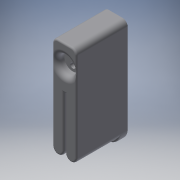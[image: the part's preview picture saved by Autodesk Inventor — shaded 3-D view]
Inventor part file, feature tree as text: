
AUTODESK INVENTOR PART (.ipt)
format: ipt  version: 2019 (Build 230136000, 136)  size: 194,560 bytes
history: native  units: mm
features: fillet x4, extrude x3, sketch x3
ambient origin geometry x8: Origin, YZ Plane, XZ Plane, XY Plane, X Axis, Y Axis, Z Axis, Center Point
bodies: Solid1 (feature_tree)
feature tree (10):
  extrude  "Extrusion1"  Depth=3.5mm
  extrude  "Extrusion2"  Depth=3.0mm
  fillet  "Fillet1"  Radius=42.75mm
  fillet  "Fillet2"  Radius=18.2mm
  fillet  "Fillet3"  Radius=7.0mm
  extrude  "Extrusion3"  Depth=3.0mm
  fillet  "Fillet4"  [1 undecoded]
  sketch  "Sketch1"  dims[d0=0.5mm d1=3.5mm]
  sketch  "Sketch2"  dims[d2=3.0mm d3=3.0mm d4=42.75mm d5=18.2mm d6=7.0mm]
  sketch  "Sketch3"  dims[d7=55.0mm d8=55.0mm d9=90.0deg d10=30.0mm d11=0.0mm d12=15.0mm d13=0.5mm d14=0.5mm d19=25.0mm d20=0.0mm d21=1.0mm d22=1.0mm d23=3.0mm d24=10.0mm d25=5.0mm d26=0.0mm d27=3.0mm]
note: 1 required parameter value undecoded (feature->parameter linkage not recoverable at this tier; creation-order binding heuristic only, values carry confidence <= 0.55)
